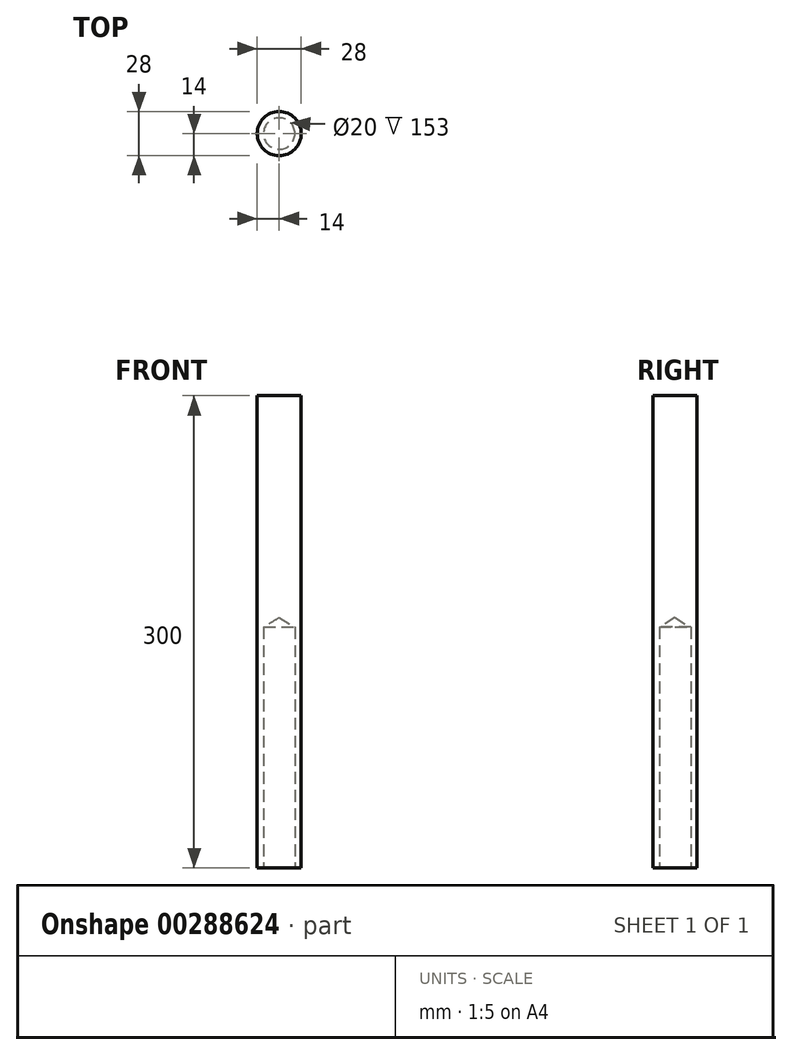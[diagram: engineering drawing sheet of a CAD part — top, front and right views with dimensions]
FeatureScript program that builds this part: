
annotation { "Feature Type Name" : "Feature", "Feature Type Description" : "" }
export const myFeature = defineFeature(function(context is Context, id is Id, definition is map)
    precondition{}
    {
        {
            var Q0;
            Q0=qCreatedBy(makeId("Top.planeOp"),FACE);
            var sketch = newSketch(context, id + "F0", { "sketchPlane" : qUnion([Q0])});
            skCircle(sketch, "E0", {"center": v(0, 0) * mm, "radius": 14 * mm});
            skSolve(sketch);
        }
        {
            var Q0;
            Q0=makeQuery(id+"F0.imprint","IMPRINT",FACE,{"disambiguationData":[TD([[makeQuery(id+"F0.imprint","IMPRINT",EDGE,{"derivedFrom":sQuery(id+"F0.wireOp",EDGE,"E0")}),1.0]])]});
            extrude(context, id + "F1", {"entities" : qUnion([Q0]), "depth" : 300 * mm});
        }
        {
            var Q0;
            Q0=makeQuery(id+"F1.opExtrude","CAP_FACE",FACE,{"disambiguationData":[OSD([sQuery(id+"F0.wireOp",EDGE,"E0"),sQuery(id+"F0.wireOp",EDGE,"8ww4Y2DM-KXoR-rVzc-PEXZ-fRz4pelTuZVR"),sQuery(id+"F0.wireOp",EDGE,"ZfQWgHuL-rbqE-vbqI-c3Jn-zyrbhTXmNbAU")])],"isStart":true});
            var sketch = newSketch(context, id + "F2", { "sketchPlane" : qUnion([Q0])});
            skPoint(sketch, "E1", {"position": v(0, 0) * mm});
            skSolve(sketch);
        }
        {
            var Q0;
            Q0=sQuery(id+"F2.wireOp",VERTEX,"E1");
            var Q1;
            Q1=makeQuery(id+"F1.opExtrude","SWEPT_BODY",BODY,{"disambiguationData":[OSD([sQuery(id+"F0.wireOp",EDGE,"E0"),sQuery(id+"F0.wireOp",EDGE,"8ww4Y2DM-KXoR-rVzc-PEXZ-fRz4pelTuZVR"),sQuery(id+"F0.wireOp",EDGE,"ZfQWgHuL-rbqE-vbqI-c3Jn-zyrbhTXmNbAU")])]});
            hole(context, id + "F3", {"style" : HoleStyle.SIMPLE, "endStyle" : HoleEndStyle.BLIND, "holeDiameter" : 20 * mm, "holeDepth" : 153 * mm, "tappedDepth" : 12 * mm, "tapClearance" : 3, "locations" : qUnion([Q0]), "scope" : qUnion([Q1])});
        }
    });
